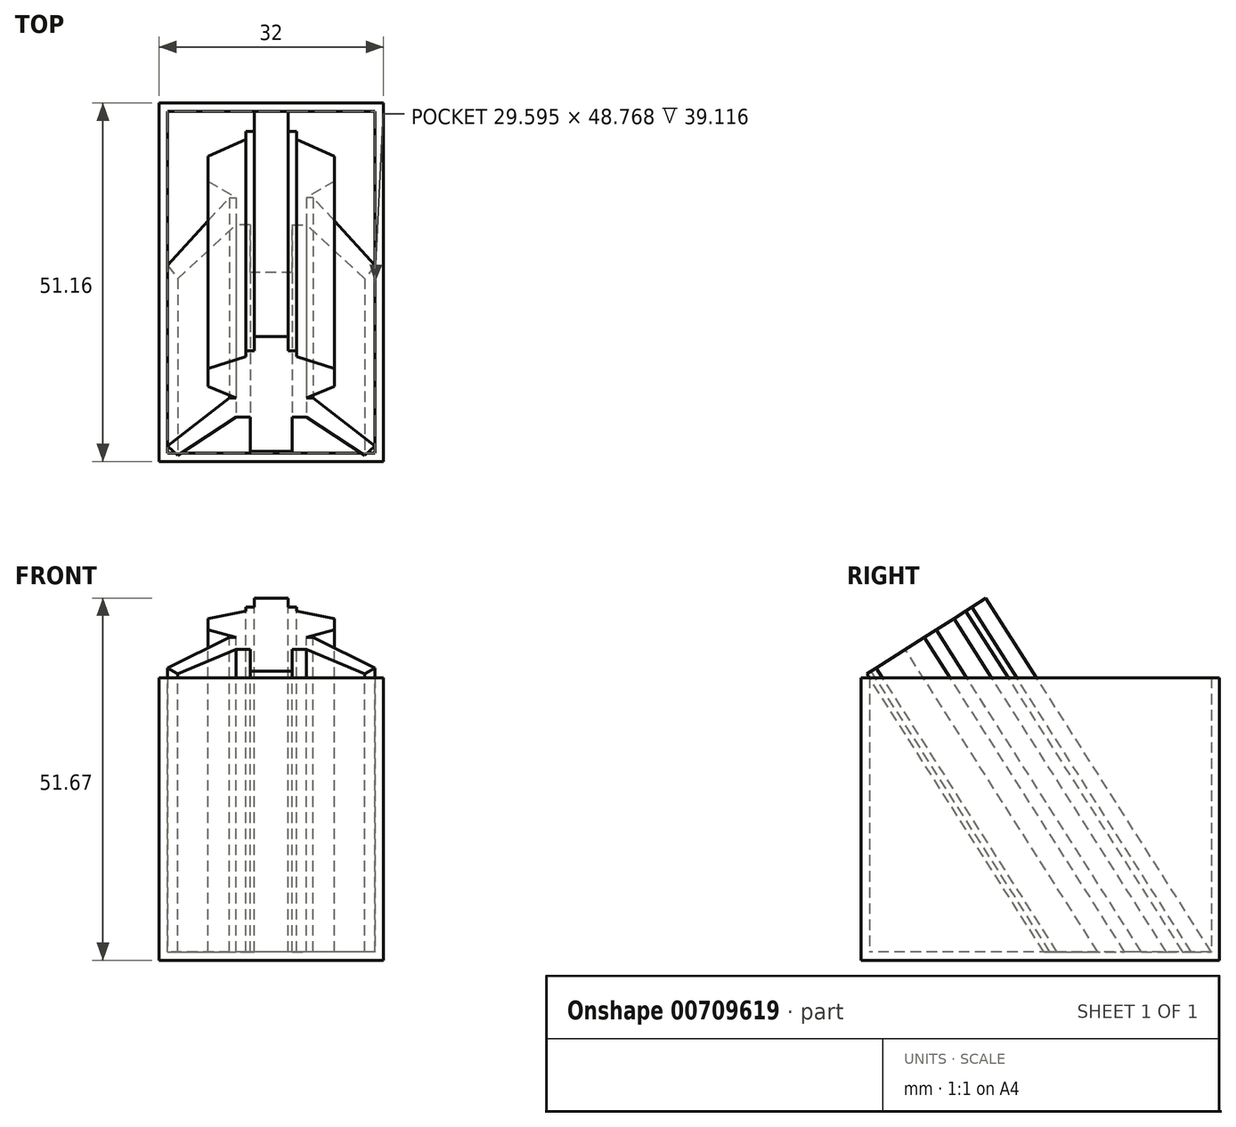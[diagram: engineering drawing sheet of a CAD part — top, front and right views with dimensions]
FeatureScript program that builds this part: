
annotation { "Feature Type Name" : "Feature", "Feature Type Description" : "" }
export const myFeature = defineFeature(function(context is Context, id is Id, definition is map)
    precondition{}
    {
        {
            var Q0;
            Q0=qCreatedBy(makeId("Top.planeOp"),FACE);
            var sketch = newSketch(context, id + "F0", { "sketchPlane" : qUnion([Q0])});
            skLineSegment(sketch, "E0.bottom", {"start": v(16, 25.58) * mm, "end": v(-16, 25.58) * mm});
            skLineSegment(sketch, "E0.top", {"start": v(16, -25.58) * mm, "end": v(-16, -25.58) * mm});
            skLineSegment(sketch, "E0.left", {"start": v(16, 25.58) * mm, "end": v(16, -25.58) * mm});
            skLineSegment(sketch, "E0.right", {"start": v(-16, 25.58) * mm, "end": v(-16, -25.58) * mm});
            skPoint(sketch, "E0.middle", {"position": v(0, 0) * mm});
            skSolve(sketch);
        }
        {
            var Q0;
            Q0=makeQuery(id+"F0.imprint","IMPRINT",FACE,{"disambiguationData":[TD([[makeQuery(id+"F0.imprint","IMPRINT",EDGE,{"derivedFrom":sQuery(id+"F0.wireOp",EDGE,"E0.bottom")}),1.0]])]});
            extrude(context, id + "F1", {"entities" : qUnion([Q0]), "depth" : 40.32 * mm, "offsetDistance" : 25 * mm, "symmetric" : true});
        }
        {
            var Q0;
            Q0=makeQuery(id+"F1.opExtrude","CAP_EDGE",EDGE,{"disambiguationData":[OSD([sQuery(id+"F0.wireOp",EDGE,"E0.top")])],"isStart":false});
            cPlane(context, id + "F2", {"entities" : qUnion([Q0]), "cplaneType" : CPlaneType.LINE_ANGLE, "offset" : 25 * mm, "angle" : 57.5 * degree, "width" : 150 * mm, "height" : 150 * mm});
        }
        {
            var Q0;
            Q0=makeQuery(id+"F1.opExtrude","CAP_FACE",FACE,{"disambiguationData":[OSD([sQuery(id+"F0.wireOp",EDGE,"E0.bottom"),sQuery(id+"F0.wireOp",EDGE,"E0.top"),sQuery(id+"F0.wireOp",EDGE,"E0.left"),sQuery(id+"F0.wireOp",EDGE,"E0.right")])],"isStart":false});
            shell(context, id + "F3", {"entities" : qUnion([Q0]), "thickness" : 1.2 * mm});
        }
        {
            var Q0;
            Q0=qCreatedBy(id+"F2.planeOp",FACE);
            var sketch = newSketch(context, id + "F4", { "sketchPlane" : qUnion([Q0])});
            skLineSegment(sketch, "E1", {"start": v(5, -3.26) * mm, "end": v(3, -3.26) * mm});
            skLineSegment(sketch, "E2", {"start": v(3, -3.26) * mm, "end": v(3, -9.02) * mm});
            skLineSegment(sketch, "E3", {"start": v(5, -0.02) * mm, "end": v(9, 1.98) * mm});
            skLineSegment(sketch, "E4", {"start": v(9, 4.98) * mm, "end": v(9, 1.98) * mm});
            skLineSegment(sketch, "E5", {"start": v(3, -9.02) * mm, "end": v(0, -9.02) * mm});
            skLineSegment(sketch, "E6", {"start": v(5, -0.02) * mm, "end": v(6, -0.02) * mm});
            skPoint(sketch, "E7", {"position": v(14.8, -8.15) * mm});
            skPoint(sketch, "E8", {"position": v(13.33, -9.74) * mm});
            skLineSegment(sketch, "E9", {"start": v(5, -3.26) * mm, "end": v(13.33, -9.74) * mm});
            skLineSegment(sketch, "E10", {"start": v(6, -0.02) * mm, "end": v(14.8, -8.15) * mm});
            skLineSegment(sketch, "E11", {"start": v(13.33, -9.74) * mm, "end": v(14.8, -8.15) * mm});
            skLineSegment(sketch, "E12", {"start": v(0, 10.38) * mm, "end": v(2.4, 10.38) * mm});
            skLineSegment(sketch, "E13", {"start": v(2.4, 10.38) * mm, "end": v(2.4, 7.98) * mm});
            skLineSegment(sketch, "E14", {"start": v(2.4, 7.98) * mm, "end": v(3.6, 7.98) * mm});
            skLineSegment(sketch, "E15", {"start": v(3.6, 7.98) * mm, "end": v(3.6, 6.98) * mm});
            skLineSegment(sketch, "E16", {"start": v(3.6, 6.98) * mm, "end": v(9, 4.98) * mm});
            skLineSegment(sketch, "E17.MirrorCS", {"start": v(-13.33, -9.74) * mm, "end": v(-14.8, -8.15) * mm});
            skLineSegment(sketch, "E18.MirrorCS", {"start": v(-3.6, 7.98) * mm, "end": v(-3.6, 6.98) * mm});
            skLineSegment(sketch, "E19.MirrorCS", {"start": v(-2.4, 7.98) * mm, "end": v(-3.6, 7.98) * mm});
            skLineSegment(sketch, "E20.MirrorCS", {"start": v(-5, -0.02) * mm, "end": v(-6, -0.02) * mm});
            skLineSegment(sketch, "E21.MirrorCS", {"start": v(-5, -3.26) * mm, "end": v(-3, -3.26) * mm});
            skLineSegment(sketch, "E22.MirrorCS", {"start": v(-2.4, 10.38) * mm, "end": v(-2.4, 7.98) * mm});
            skLineSegment(sketch, "E23.MirrorCS", {"start": v(-3, -3.26) * mm, "end": v(-3, -9.02) * mm});
            skLineSegment(sketch, "E24.MirrorCS", {"start": v(-6, -0.02) * mm, "end": v(-14.8, -8.15) * mm});
            skLineSegment(sketch, "E25.MirrorCS", {"start": v(-3, -9.02) * mm, "end": v(0, -9.02) * mm});
            skLineSegment(sketch, "E26.MirrorCS", {"start": v(-3.6, 6.98) * mm, "end": v(-9, 4.98) * mm});
            skLineSegment(sketch, "E27.MirrorCS", {"start": v(-5, -3.26) * mm, "end": v(-13.33, -9.74) * mm});
            skLineSegment(sketch, "E28.MirrorCS", {"start": v(-9, 4.98) * mm, "end": v(-9, 1.98) * mm});
            skLineSegment(sketch, "E29.MirrorCS", {"start": v(-5, -0.02) * mm, "end": v(-9, 1.98) * mm});
            skLineSegment(sketch, "E30.MirrorCS", {"start": v(0, 10.38) * mm, "end": v(-2.4, 10.38) * mm});
            skPoint(sketch, "E31.MirrorP", {"position": v(-14.8, -8.15) * mm});
            skPoint(sketch, "E32.MirrorP", {"position": v(-13.33, -9.74) * mm});
            skLineSegment(sketch, "E33", {"start": v(0, -9.02) * mm, "end": v(0, -9.74) * mm, "construction": true});
            skSolve(sketch);
        }
        {
            var Q0;
            Q0=makeQuery(id+"F4.imprint","IMPRINT",FACE,{"disambiguationData":[TD([[makeQuery(id+"F4.imprint","IMPRINT",EDGE,{"derivedFrom":sQuery(id+"F4.wireOp",EDGE,"E1")}),-1.0]])]});
            var Q1;
            Q1=makeQuery(id+"F3.opShell","OFFSET_FACE",FACE,{"disambiguationData":[OSD([sQuery(id+"F0.wireOp",EDGE,"E0.bottom"),sQuery(id+"F0.wireOp",EDGE,"E0.top"),sQuery(id+"F0.wireOp",EDGE,"E0.left"),sQuery(id+"F0.wireOp",EDGE,"E0.right")])]});
            extrude(context, id + "F5", {"entities" : qUnion([Q0]), "endBound" : BoundingType.UP_TO_SURFACE, "oppositeDirection" : true, "depth" : 25 * mm, "endBoundEntityFace" : qUnion([Q1]), "offsetDistance" : 25 * mm});
        }
    });
